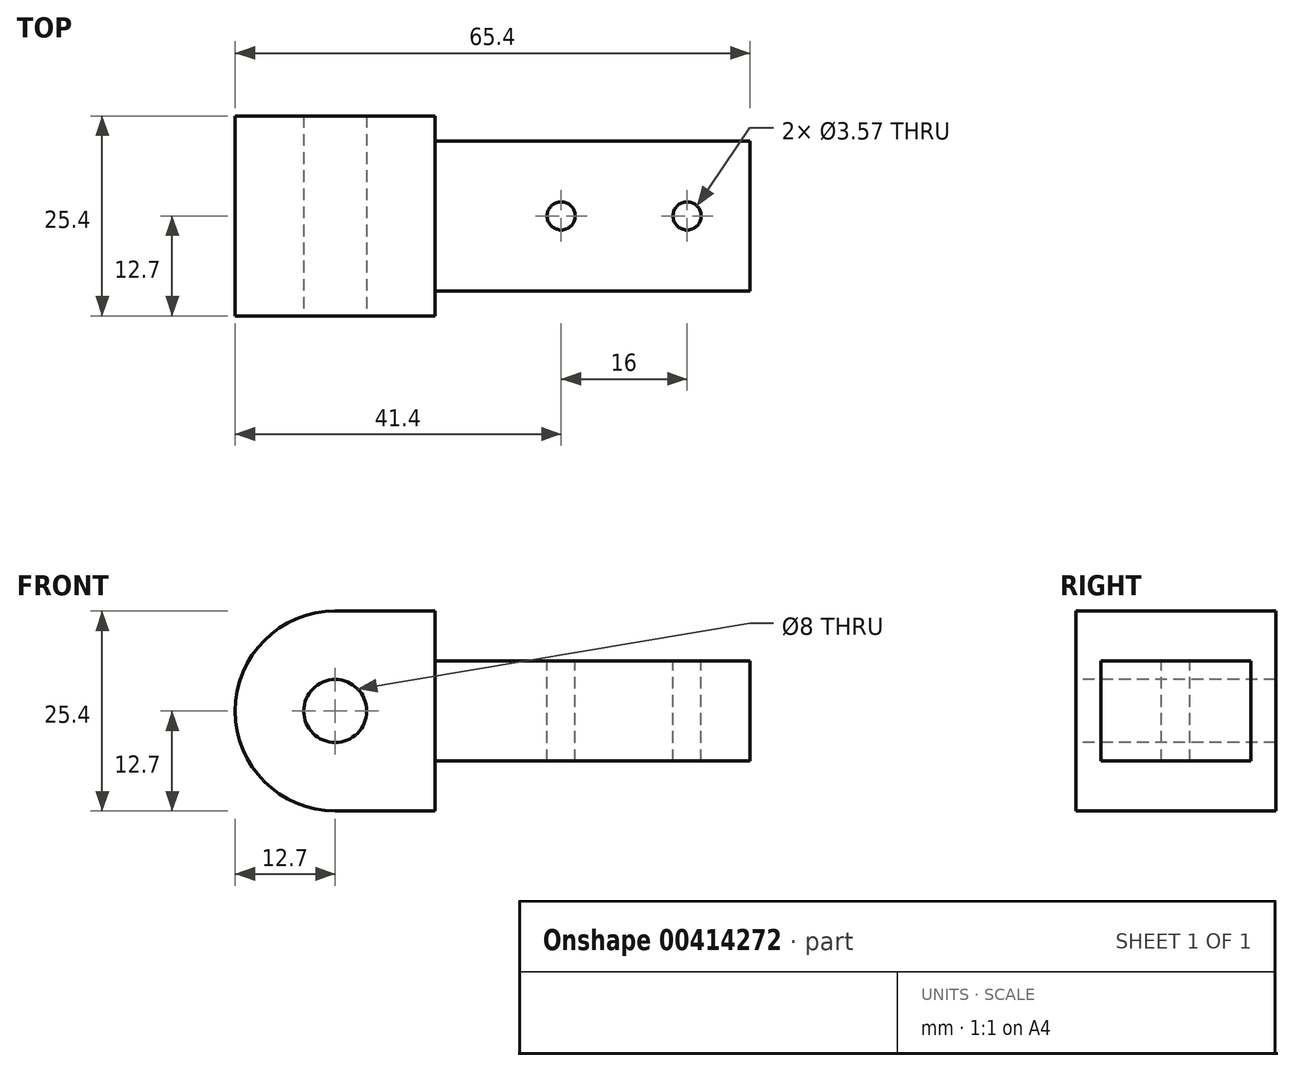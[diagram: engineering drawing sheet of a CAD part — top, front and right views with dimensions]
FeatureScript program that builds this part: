
annotation { "Feature Type Name" : "Feature", "Feature Type Description" : "" }
export const myFeature = defineFeature(function(context is Context, id is Id, definition is map)
    precondition{}
    {
        {
            var Q0;
            Q0=qCreatedBy(makeId("Top.planeOp"),FACE);
            var sketch = newSketch(context, id + "F0", { "sketchPlane" : qUnion([Q0])});
            skLineSegment(sketch, "E0.bottom", {"start": v(20, 9.53) * mm, "end": v(-20, 9.53) * mm});
            skLineSegment(sketch, "E0.top", {"start": v(20, -9.52) * mm, "end": v(-20, -9.52) * mm});
            skLineSegment(sketch, "E0.left", {"start": v(20, 9.53) * mm, "end": v(20, -9.52) * mm});
            skLineSegment(sketch, "E0.right", {"start": v(-20, 9.53) * mm, "end": v(-20, -9.53) * mm});
            skPoint(sketch, "E0.middle", {"position": v(0, 0) * mm});
            skSolve(sketch);
        }
        {
            var Q0;
            Q0=makeQuery(id+"F0.imprint","IMPRINT",FACE,{"disambiguationData":[TD([[makeQuery(id+"F0.imprint","IMPRINT",EDGE,{"derivedFrom":sQuery(id+"F0.wireOp",EDGE,"E0.bottom")}),1.0]])]});
            extrude(context, id + "F1", {"entities" : qUnion([Q0]), "depth" : 12.7 * mm});
        }
        {
            var Q0;
            Q0=makeQuery(id+"F1.opExtrude","SWEPT_FACE",FACE,{"disambiguationData":[OSD([sQuery(id+"F0.wireOp",EDGE,"E0.right")])]});
            var sketch = newSketch(context, id + "F2", { "sketchPlane" : qUnion([Q0])});
            skLineSegment(sketch, "E1.bottom", {"start": v(12.7, 19.05) * mm, "end": v(-12.7, 19.05) * mm});
            skLineSegment(sketch, "E1.top", {"start": v(12.7, -6.35) * mm, "end": v(-12.7, -6.35) * mm});
            skLineSegment(sketch, "E1.left", {"start": v(12.7, 19.05) * mm, "end": v(12.7, -6.35) * mm});
            skLineSegment(sketch, "E1.right", {"start": v(-12.7, 19.05) * mm, "end": v(-12.7, -6.35) * mm});
            skPoint(sketch, "E1.middle", {"position": v(0, 6.35) * mm});
            skSolve(sketch);
        }
        {
            var Q0;
            {var subQ0=sQuery(id+"F0.wireOp",EDGE,"E0.right");Q0=makeQuery(id+"F2.imprint","IMPRINT",FACE,{"disambiguationData":[TD([[makeQuery(id+"F2.imprint","IMPRINT",EDGE,{"derivedFrom":makeQuery(id+"F1.opExtrude","CAP_EDGE",EDGE,{"disambiguationData":[OSD([subQ0])],"isStart":true})}),1.0]])]});}
            var Q1;
            Q1=makeQuery(id+"F2.imprint","IMPRINT",FACE,{"disambiguationData":[TD([[makeQuery(id+"F2.imprint","IMPRINT",EDGE,{"derivedFrom":sQuery(id+"F2.wireOp",EDGE,"E1.bottom")}),1.0]])]});
            extrude(context, id + "F3", {"entities" : qUnion([Q0, Q1]), "operationType" : NewBodyOperationType.ADD, "depth" : 25.4 * mm});
        }
        {
            var Q0;
            Q0=makeQuery(id+"F3.opExtrude","SWEPT_FACE",FACE,{"disambiguationData":[OSD([sQuery(id+"F2.wireOp",EDGE,"E1.left")])]});
            var sketch = newSketch(context, id + "F4", { "sketchPlane" : qUnion([Q0])});
            skPoint(sketch, "E2", {"position": v(-32.7, 6.35) * mm});
            skSolve(sketch);
        }
        {
            var Q0;
            Q0=sQuery(id+"F4.wireOp",VERTEX,"E2");
            var Q1;
            Q1=makeQuery(id+"F1.opExtrude","SWEPT_BODY",BODY,{"disambiguationData":[OSD([sQuery(id+"F0.wireOp",EDGE,"E0.bottom"),sQuery(id+"F0.wireOp",EDGE,"E0.top"),sQuery(id+"F0.wireOp",EDGE,"E0.left"),sQuery(id+"F0.wireOp",EDGE,"E0.right")])]});
            hole(context, id + "F5", {"style" : HoleStyle.SIMPLE, "endStyle" : HoleEndStyle.THROUGH, "holeDiameter" : 8 * mm, "isTappedThrough" : true, "tappedDepth" : 12.7 * mm, "tapClearance" : 3, "locations" : qUnion([Q0]), "scope" : qUnion([Q1])});
        }
        {
            var Q0;
            Q0=makeQuery(id+"F3.opExtrude","CAP_EDGE",EDGE,{"disambiguationData":[OSD([sQuery(id+"F2.wireOp",EDGE,"E1.bottom")])],"isStart":false});
            var Q1;
            Q1=makeQuery(id+"F3.opExtrude","CAP_EDGE",EDGE,{"disambiguationData":[OSD([sQuery(id+"F2.wireOp",EDGE,"E1.top")])],"isStart":false});
            fillet(context, id + "F6", {"entities" : qUnion([Q0, Q1]), "radius" : 12.7 * mm, "tangentPropagation" : true, "allowEdgeOverflow" : false});
        }
        {
            var Q0;
            Q0=makeQuery(id+"F1.opExtrude","CAP_FACE",FACE,{"disambiguationData":[OSD([sQuery(id+"F0.wireOp",EDGE,"E0.bottom"),sQuery(id+"F0.wireOp",EDGE,"E0.top"),sQuery(id+"F0.wireOp",EDGE,"E0.left"),sQuery(id+"F0.wireOp",EDGE,"E0.right")])],"isStart":false});
            var sketch = newSketch(context, id + "F7", { "sketchPlane" : qUnion([Q0])});
            skPoint(sketch, "E3", {"position": v(12, 0) * mm});
            skPoint(sketch, "E4", {"position": v(-4, 0) * mm});
            skSolve(sketch);
        }
        {
            var Q0;
            Q0=sQuery(id+"F7.wireOp",VERTEX,"E3");
            var Q1;
            Q1=sQuery(id+"F7.wireOp",VERTEX,"E4");
            var Q2;
            Q2=makeQuery(id+"F1.opExtrude","SWEPT_BODY",BODY,{"disambiguationData":[OSD([sQuery(id+"F0.wireOp",EDGE,"E0.bottom"),sQuery(id+"F0.wireOp",EDGE,"E0.top"),sQuery(id+"F0.wireOp",EDGE,"E0.left"),sQuery(id+"F0.wireOp",EDGE,"E0.right")])]});
            hole(context, id + "F8", {"style" : HoleStyle.SIMPLE, "endStyle" : HoleEndStyle.THROUGH, "holeDiameter" : 3.57 * mm, "isTappedThrough" : true, "tappedDepth" : 12.7 * mm, "tapClearance" : 3, "locations" : qUnion([Q0, Q1]), "scope" : qUnion([Q2])});
        }
    });
